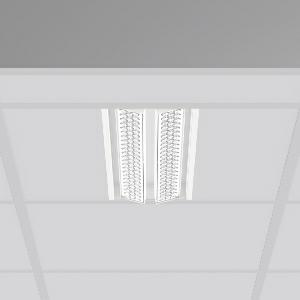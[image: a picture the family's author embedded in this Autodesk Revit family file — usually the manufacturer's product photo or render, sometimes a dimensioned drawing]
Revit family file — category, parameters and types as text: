
# Revit family: tx-move_901733_002_1_76_44e6
name_source: partatom
category: Lighting Fixtures
units: mm (PartAtom-declared; Revit-internal decimal feet)

## family parameters
Cut with Voids When Loaded = No
Host = Face
Light Source = No
Part Type = Normal
Room Calculation Point = No
Round Connector Dimension = Use Diameter
Shared = No

## types (1)
- MultiLumen 1 (1 x LED Modul 840, 2850 lm, 4000)
    Apparent Load = 35 VA
    Approval mark = CE
    CIE Flux Codes = 77 96 99 100 100
    Color Rendering = 80
    Color Temperature = 4000
    Default Elevation = 1800 mm
    Description = Series: TX-MOVE
Einlege/Einbau-Flächenstrahler. Housing: sheet steel, powder-coated. 2xSwivel range: 90°. High-efficiency LED units with optimum light control thanks to clear plastic (PC) lens optics. Spezielle Mikrostrukturen reduzieren Gelbsaum. Symmetrical light distribution. Suitable for laying in grid ceiling module 600. Connected converter included in separate gearbox.Suitable for through-wiring.MultiLumen: Luminous flux adjustable in 3 steps. Accessories: Mounting frame for installation in suspended ceilings. Environmentally friendly and resource-saving due to replaceable and recyclable components. 
Colour: traffic white, matt (RAL 9016)
Length: 597 mm
Width: 190 mm
Height: 39 mm
Cut-out length: 577.5 mm
Cut-out width: 174 mm
Recess height: 100 mm
Lamp: LED
Socket: without socket
Colour temperature: 4000K
Colour rendering index (CRI): 80
System power: 35 W
Rated luminous flux: 5700 lm
Luminous efficiency: 163 lm/W
System power 2: 47 W
Rated luminous flux 2: 7450 lm
Luminous efficiency 2: 159 lm/W
System power 3: 68 W
Rated luminous flux 3: 10200 lm
Luminous efficiency 3: 150 lm/W
Control gear: Dimmable EVG, DALI
Protection class: I
Type of protection: IP 20
    Height = 0 mm  [stored 0 ft]
    Lamp = 1 x LED Modul 840
    Lamp Light Flux = 2850 lm
    Lamp count = 1
    Length = 597 mm
    Lifetime = 50000 h
    Luminous efficacy = 163 lm/W
    Manufacturer = RZB
    ModVariant = No
    Model = 901733.002.1.76
    Mounting Place = Ceiling, Wall
    Mounting Type = Recessed
    Number of Poles = 1
    OnlyDefault = Yes
    Power Factor = 1
    Product Name = TX-MOVE
    Product group = Recessed projectors
    ProductGroupID = 401
    Protection Class = Protection class I
    Protection Degree = IP 20
    RLX_Detail_Level = 1
    RLX_Emergency_Light_Flux = 0 lm
    RLX_Emergency_Type = 0
    RLX_Emergency_Type_DB = No
    RlxData = <blob elided: 35429 chars, md5=76681f43>
    Socket = socket
    Standby Power = 0 W
    System Light Flux = 5700 lm
    System Power = 35 W
    Type Comments = MultiLumen 1
    Type Image = 901733.002.jpg
    URL = http://relux.com
    VarID = multilumen_1
    Voltage = 230 V
    Voltage Range = 220-240 V
    Weight = 0.00 kg
    Width = 190 mm

note: [stored X ft] marks values corroborated as IEEE doubles in the binary element streams (Revit-internal decimal feet)

## geometry (parser evidence)
native form markers: Blend x4, Sweep x12
no freeform markers — native parametric forms only
